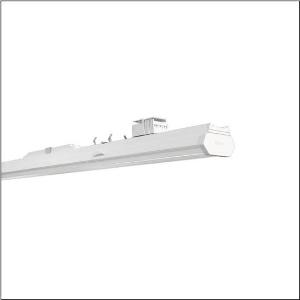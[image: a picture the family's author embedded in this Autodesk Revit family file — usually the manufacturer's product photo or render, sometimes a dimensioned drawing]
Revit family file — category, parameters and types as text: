
# Revit family: licross_r__11_protected_mo_51tp12dn495gd_6c21
name_source: partatom
category: Lighting Fixtures
units: mm (PartAtom-declared; Revit-internal decimal feet)

## family parameters
Cut with Voids When Loaded = No
Host = Face
Light Source = No
Part Type = Normal
Room Calculation Point = No
Round Connector Dimension = Use Diameter
Shared = No

## types (1)
- --- (1 x LED, 1500 lm, 9.3 W, 4000K)
    Apparent Load = 9 VA
    CIE Flux Codes = 73 92 98 99 100
    Color Rendering = 80
    Color Temperature = 4000K
    Default Elevation = 1800 mm
    Description = Licross® 11 Protected MO, luminaire insert, of sheet steel, galvanised, coil coated, white, length: 1.500mm, width: 90mm, height: 101mm, LED rated luminous flux: 9.980lm, light colour: 840, control gear: DALI 2 (for two DALI lines), with plug, 6-pole, with phase selection, mains connection: 220..240V, AC/DC, 0/50..60Hz, rated input power: 57W, halogen-free wiring, for central battery installations according to DIN EN 60598-2-22, for emergency light function, without changeover relay, primary optical cover: cover, of PMMA, light emission: direct distribution, primary light characteristic: symmetric, protection rating (complete): IP64, insulation class (complete): insulation class I (protective earthing), certification: CE, ENEC, VDE, UKCA, protection symbol: D if used in an environment with conductive dust loads with corresponding accessories, impact resistance: IK06, permissible ambient temperature for indoor applications: -25..+35°C, standard: EN 60598-2-22, corresponds to IFS (International Featured Standards) requirements for safety and quality in the food industry, reducing of maximum allowable ambient temperature of 5°C with ceiling mounting, LABS conformity tested according to VDMA 24364:2018-05, packaging unit: 1 piece
    Height = 92 mm
    Lamp = 1 x LED
    Lamp Light Flux = 1500 lm
    Lamp Power = 9.3 W
    Lamp count = 1
    Length = 1500 mm  [stored 4.92126 ft]
    Luminous efficacy = 161 lm/W
    Manufacturer = Siteco
    ModVariant = No
    Model = 51TP12DN495GD
    Mounting Place = Ceiling
    Mounting Type = Pendant
    Number of Poles = 1
    OnlyDefault = Yes
    Power Factor = 1
    Product Name = Licross® 11 Protected MO
    Product group = luminaire insert
    ProductGroupID = 901
    Protection Class = Protection class I
    Protection Degree = IP 64
    RLX_Detail_Level = 1
    RLX_Emergency_Light_Flux = 0 lm
    RLX_Emergency_Type = 0
    RLX_Emergency_Type_DB = No
    RlxData = <blob elided: 24773 chars, md5=fec3ce2a>
    Socket = socket
    Standby Power = 0 W
    System Light Flux = 1500 lm
    System Power = 9 W
    Type Comments = : DC mode (central or group accumulator) initial emergency light level
    Type Image = l_1256148.jpg
    URL = http://relux.com
    VarID = @adj_056513
    Voltage = 0 V
    Weight = 0.00 kg
    Width = 88 mm

note: [stored X ft] marks values corroborated as IEEE doubles in the binary element streams (Revit-internal decimal feet)

## geometry (parser evidence)
native form markers: Blend x4, Sweep x10
no freeform markers — native parametric forms only
